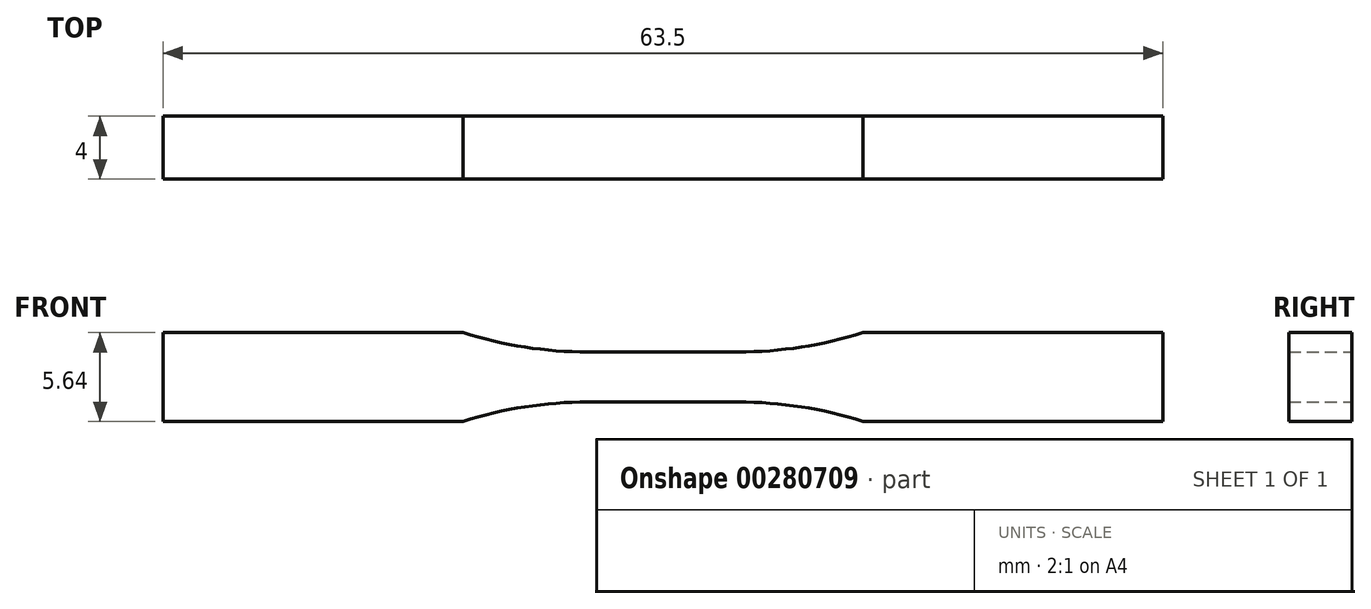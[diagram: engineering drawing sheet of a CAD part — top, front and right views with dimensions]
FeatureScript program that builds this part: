
annotation { "Feature Type Name" : "Feature", "Feature Type Description" : "" }
export const myFeature = defineFeature(function(context is Context, id is Id, definition is map)
    precondition{}
    {
        {
            var Q0;
            Q0=qCreatedBy(makeId("Front.planeOp"),FACE);
            var sketch = newSketch(context, id + "F0", { "sketchPlane" : qUnion([Q0])});
            skLineSegment(sketch, "E0", {"start": v(0, 1.6) * mm, "end": v(4.77, 1.6) * mm});
            skArc(sketch, "E1", {"start": v(4.77, 1.6) * mm, "mid": v(8.78, 1.9) * mm, "end": v(12.7, 2.82) * mm});
            skLineSegment(sketch, "E2", {"start": v(12.7, 2.82) * mm, "end": v(31.75, 2.82) * mm});
            skLineSegment(sketch, "E3", {"start": v(31.75, 2.82) * mm, "end": v(31.75, 0) * mm});
            skLineSegment(sketch, "E4.MirrorCS", {"start": v(0, 1.6) * mm, "end": v(-4.77, 1.6) * mm});
            skLineSegment(sketch, "E5.MirrorCS", {"start": v(-31.75, 2.82) * mm, "end": v(-31.75, 0) * mm});
            skLineSegment(sketch, "E6.MirrorCS", {"start": v(-12.7, 2.82) * mm, "end": v(-31.75, 2.82) * mm});
            skArc(sketch, "E7.MirrorCS", {"start": v(-4.77, 1.6) * mm, "mid": v(-8.78, 1.9) * mm, "end": v(-12.7, 2.82) * mm});
            skArc(sketch, "E8.MirrorCS", {"start": v(-4.77, -1.6) * mm, "mid": v(-8.78, -1.9) * mm, "end": v(-12.7, -2.82) * mm});
            skLineSegment(sketch, "E9.MirrorCS", {"start": v(-12.7, -2.82) * mm, "end": v(-31.75, -2.82) * mm});
            skArc(sketch, "E10.MirrorCS", {"start": v(4.77, -1.6) * mm, "mid": v(8.78, -1.9) * mm, "end": v(12.7, -2.82) * mm});
            skLineSegment(sketch, "E11.MirrorCS", {"start": v(12.7, -2.82) * mm, "end": v(31.75, -2.82) * mm});
            skLineSegment(sketch, "E12.MirrorCS", {"start": v(-31.75, -2.82) * mm, "end": v(-31.75, 0) * mm});
            skLineSegment(sketch, "E13.MirrorCS", {"start": v(0, -1.6) * mm, "end": v(-4.77, -1.6) * mm});
            skLineSegment(sketch, "E14.MirrorCS", {"start": v(31.75, -2.82) * mm, "end": v(31.75, 0) * mm});
            skLineSegment(sketch, "E15.MirrorCS", {"start": v(0, -1.6) * mm, "end": v(4.77, -1.6) * mm});
            skSolve(sketch);
        }
        {
            var Q0;
            Q0=makeQuery(id+"F0.imprint","IMPRINT",FACE,{"disambiguationData":[TD([[makeQuery(id+"F0.imprint","IMPRINT",EDGE,{"derivedFrom":sQuery(id+"F0.wireOp",EDGE,"E0")}),-1.0]])]});
            extrude(context, id + "F1", {"entities" : qUnion([Q0]), "endBound" : BoundingType.SYMMETRIC, "depth" : 4 * mm});
        }
    });
